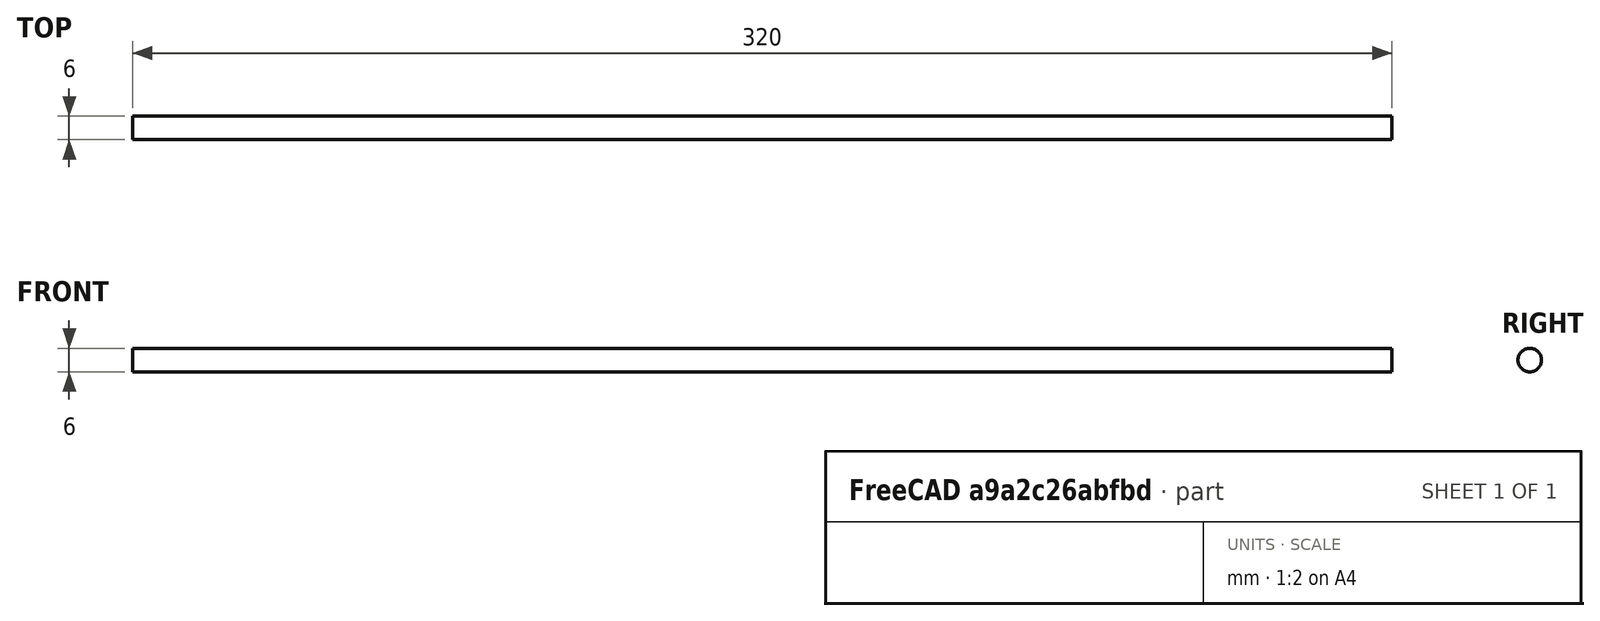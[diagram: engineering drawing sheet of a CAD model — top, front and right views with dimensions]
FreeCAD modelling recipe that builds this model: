
FCSTD DOCUMENT  (FreeCAD 0.18R15441 (Git))
Label: Rod_M6x320mm
License: All rights reserved
LicenseURL: http://en.wikipedia.org/wiki/All_rights_reserved
objects: Sketcher::SketchObject×1, PartDesign::Pad×1, PartDesign::Body×1, App::Part×1
note: 4 computed .brp shape members not serialized (recipe doc carries the construction recipe); baked Part::Feature solids carry a one-line shape summary decoded from their .brp

FEATURE [Sketcher::SketchObject] Sketch  label="RodSketch"
  MapMode = 5
  Placement = pos=(0,0,0) rot=(0.57735,0.57735,0.57735;2.0944rad)
  Support = -> [YZ_Plane001]
  sketch-geometry (1):
    g0: Circle CenterX=0 CenterY=0 CenterZ=0 NormalX=0 NormalY=0 NormalZ=1 AngleXU=0 Radius=3
  constraints (2):
    c: Coincident(g0,g-1)
    c: Radius(g0) = 3
FEATURE [PartDesign::Pad] Pad  label="RodPad"
  Length = 320
  Length2 = 100
  Midplane = true
  Placement = pos=(0,0,0) rot=(0.57735,0.57735,0.57735;2.0944rad)
  Profile = -> Sketch
  Type = 0
FEATURE [PartDesign::Body] Body  label="RodBody"
  Group = -> [Sketch,Pad]
  Origin = -> Origin001
  Tip = -> Pad
FEATURE [App::Part] Part  label="Rod_M6x320_Part"
  Group = -> [Body]
  License = CC BY 3.0
  LicenseURL = http://creativecommons.org/licenses/by/3.0/
  Origin = -> Origin
